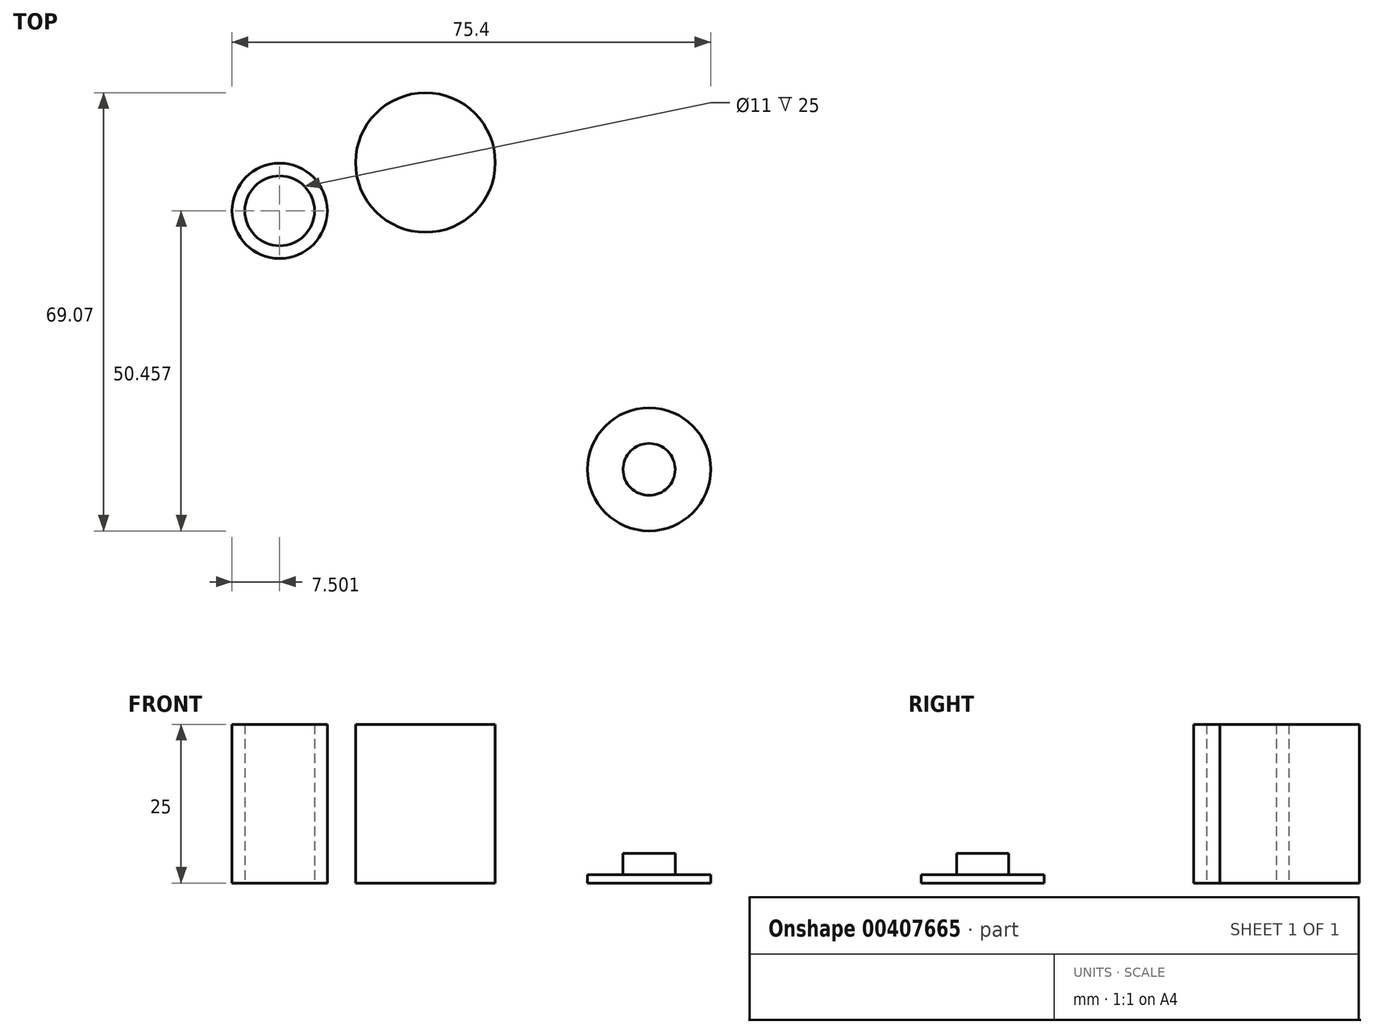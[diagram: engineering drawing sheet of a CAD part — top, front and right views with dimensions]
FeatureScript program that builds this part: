
annotation { "Feature Type Name" : "Feature", "Feature Type Description" : "" }
export const myFeature = defineFeature(function(context is Context, id is Id, definition is map)
    precondition{}
    {
        {
            var Q0;
            Q0=qCreatedBy(makeId("Top.planeOp"),FACE);
            var sketch = newSketch(context, id + "F0", { "sketchPlane" : qUnion([Q0])});
            skCircle(sketch, "E0", {"center": v(0, 0) * mm, "radius": 9.7 * mm});
            skSolve(sketch);
        }
        {
            var Q0;
            Q0 = qSketchRegion(id + "F0", true);
            extrude(context, id + "F1", {"entities" : qUnion([Q0]), "depth" : 1.3 * mm});
        }
        {
            var Q0;
            Q0=makeQuery(id+"F1.opExtrude","CAP_FACE",FACE,{"disambiguationData":[OSD([sQuery(id+"F0.wireOp",EDGE,"E0")])],"isStart":false});
            var sketch = newSketch(context, id + "F2", { "sketchPlane" : qUnion([Q0])});
            skCircle(sketch, "E1", {"center": v(0, 0) * mm, "radius": 4.1 * mm});
            skSolve(sketch);
        }
        {
            var Q0;
            Q0=makeQuery(id+"F2.imprint","IMPRINT",FACE,{"disambiguationData":[TD([[makeQuery(id+"F2.imprint","IMPRINT",EDGE,{"derivedFrom":sQuery(id+"F2.wireOp",EDGE,"E1")}),1.0]])]});
            extrude(context, id + "F3", {"entities" : qUnion([Q0]), "operationType" : NewBodyOperationType.ADD, "depth" : 3.4 * mm});
        }
        {
            var Q0;
            Q0=qCreatedBy(makeId("Top.planeOp"),FACE);
            var sketch = newSketch(context, id + "F4", { "sketchPlane" : qUnion([Q0])});
            skCircle(sketch, "E2", {"center": v(-58.2, 40.76) * mm, "radius": 5.5 * mm});
            skCircle(sketch, "E3.0", {"center": v(-58.2, 40.76) * mm, "radius": 7.5 * mm});
            skCircle(sketch, "E4", {"center": v(-35.24, 48.37) * mm, "radius": 11 * mm});
            skSolve(sketch);
        }
        {
            var Q0;
            Q0=makeQuery(id+"F4.imprint","IMPRINT",FACE,{"disambiguationData":[TD([[makeQuery(id+"F4.imprint","IMPRINT",EDGE,{"derivedFrom":sQuery(id+"F4.wireOp",EDGE,"E2")}),-1.0]])]});
            extrude(context, id + "F5", {"entities" : qUnion([Q0]), "depth" : 25 * mm, "offsetDistance" : 25 * mm});
        }
        {
            var Q0;
            Q0=makeQuery(id+"F4.imprint","IMPRINT",FACE,{"disambiguationData":[TD([[makeQuery(id+"F4.imprint","IMPRINT",EDGE,{"derivedFrom":sQuery(id+"F4.wireOp",EDGE,"E4")}),1.0]])]});
            extrude(context, id + "F6", {"entities" : qUnion([Q0]), "depth" : 25 * mm, "offsetDistance" : 25 * mm});
        }
    });
